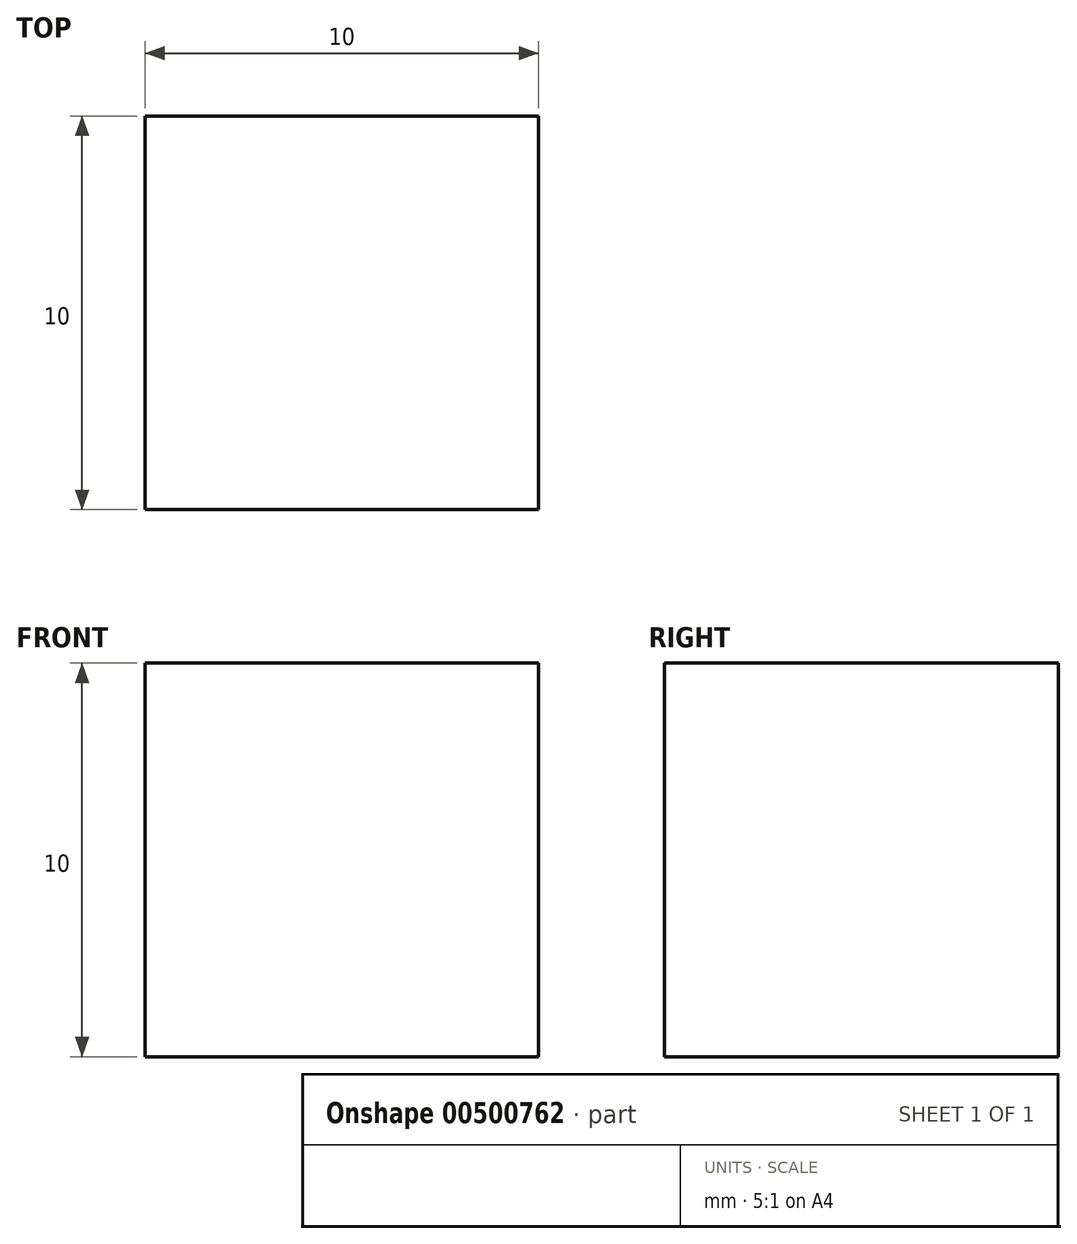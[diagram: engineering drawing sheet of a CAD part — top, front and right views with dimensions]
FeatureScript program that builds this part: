
annotation { "Feature Type Name" : "Feature", "Feature Type Description" : "" }
export const myFeature = defineFeature(function(context is Context, id is Id, definition is map)
    precondition{}
    {
        {
            var Q0;
            Q0=qCreatedBy(makeId("Top.planeOp"),FACE);
            var sketch = newSketch(context, id + "F0", { "sketchPlane" : qUnion([Q0])});
            skLineSegment(sketch, "E0.bottom", {"start": v(-5, 5) * mm, "end": v(5, 5) * mm});
            skLineSegment(sketch, "E0.top", {"start": v(-5, -5) * mm, "end": v(5, -5) * mm});
            skLineSegment(sketch, "E0.left", {"start": v(-5, 5) * mm, "end": v(-5, -5) * mm});
            skLineSegment(sketch, "E0.right", {"start": v(5, 5) * mm, "end": v(5, -5) * mm});
            skSolve(sketch);
        }
        {
            var Q0;
            Q0=makeQuery(id+"F0.imprint","IMPRINT",FACE,{"disambiguationData":[TD([[makeQuery(id+"F0.imprint","IMPRINT",EDGE,{"derivedFrom":sQuery(id+"F0.wireOp",EDGE,"E0.bottom")}),-1.0]])]});
            extrude(context, id + "F1", {"entities" : qUnion([Q0]), "depth" : 10 * mm});
        }
    });
